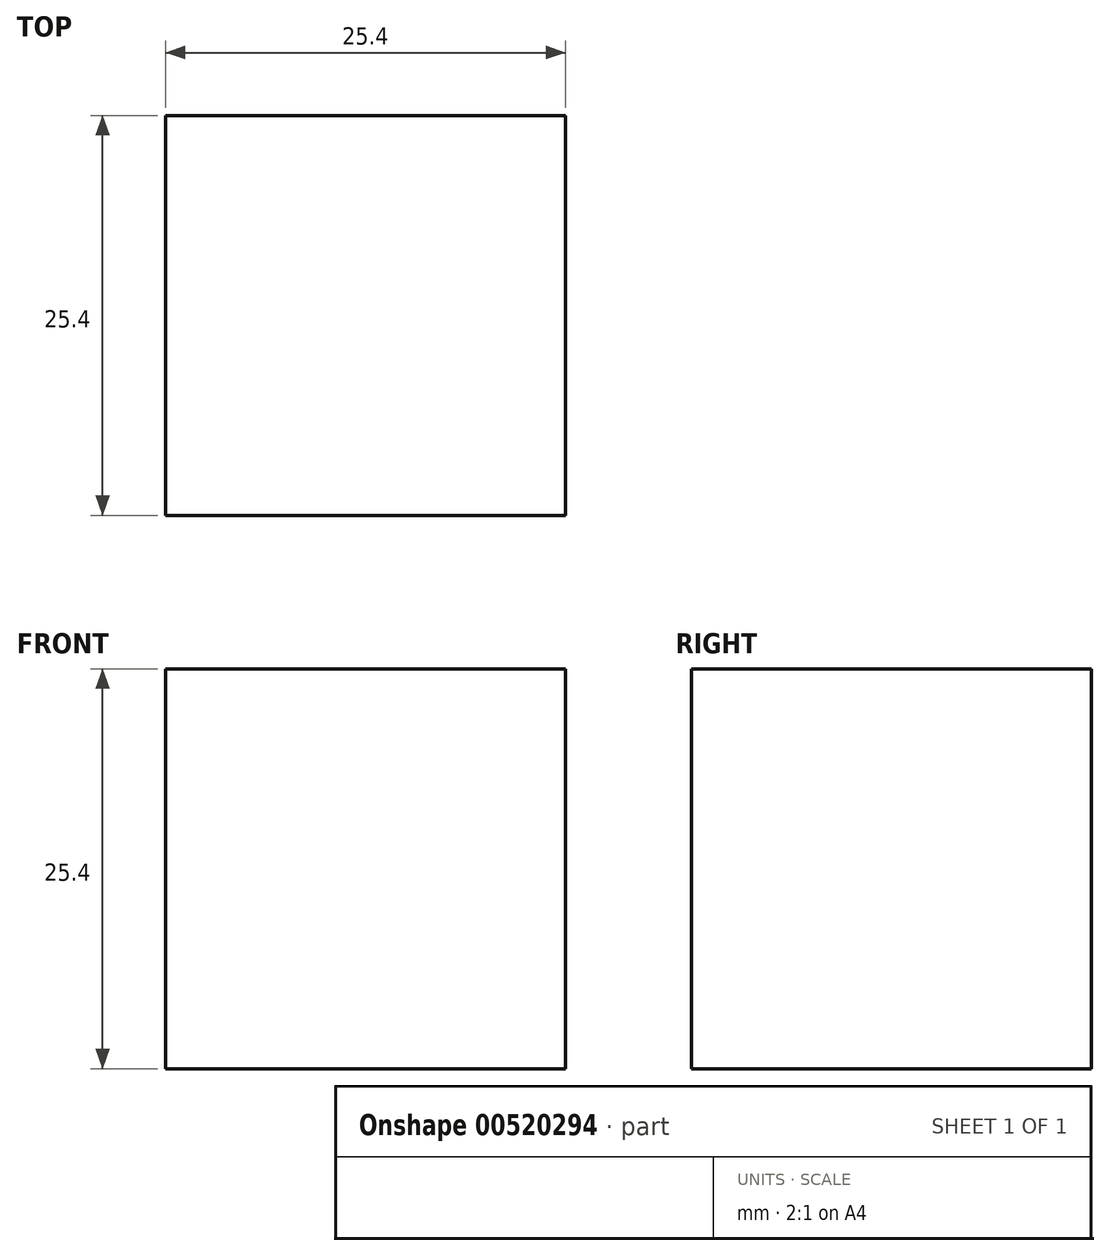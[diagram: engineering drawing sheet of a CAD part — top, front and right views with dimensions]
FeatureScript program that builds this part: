
annotation { "Feature Type Name" : "Feature", "Feature Type Description" : "" }
export const myFeature = defineFeature(function(context is Context, id is Id, definition is map)
    precondition{}
    {
        {
            var Q0;
            Q0=qCreatedBy(makeId("Front.planeOp"),FACE);
            var sketch = newSketch(context, id + "F0", { "sketchPlane" : qUnion([Q0])});
            skLineSegment(sketch, "E0.bottom", {"start": v(-25.4, 25.4) * mm, "end": v(0, 25.4) * mm});
            skLineSegment(sketch, "E0.top", {"start": v(-25.4, 0) * mm, "end": v(0, 0) * mm});
            skLineSegment(sketch, "E0.left", {"start": v(-25.4, 25.4) * mm, "end": v(-25.4, 0) * mm});
            skLineSegment(sketch, "E0.right", {"start": v(0, 25.4) * mm, "end": v(0, 0) * mm});
            skSolve(sketch);
        }
        {
            var Q0;
            Q0=makeQuery(id+"F0.imprint","IMPRINT",FACE,{"disambiguationData":[TD([[makeQuery(id+"F0.imprint","IMPRINT",EDGE,{"derivedFrom":sQuery(id+"F0.wireOp",EDGE,"E0.bottom")}),-1.0]])]});
            extrude(context, id + "F1", {"entities" : qUnion([Q0]), "depth" : 25.4 * mm, "offsetDistance" : 25.4 * mm});
        }
    });
